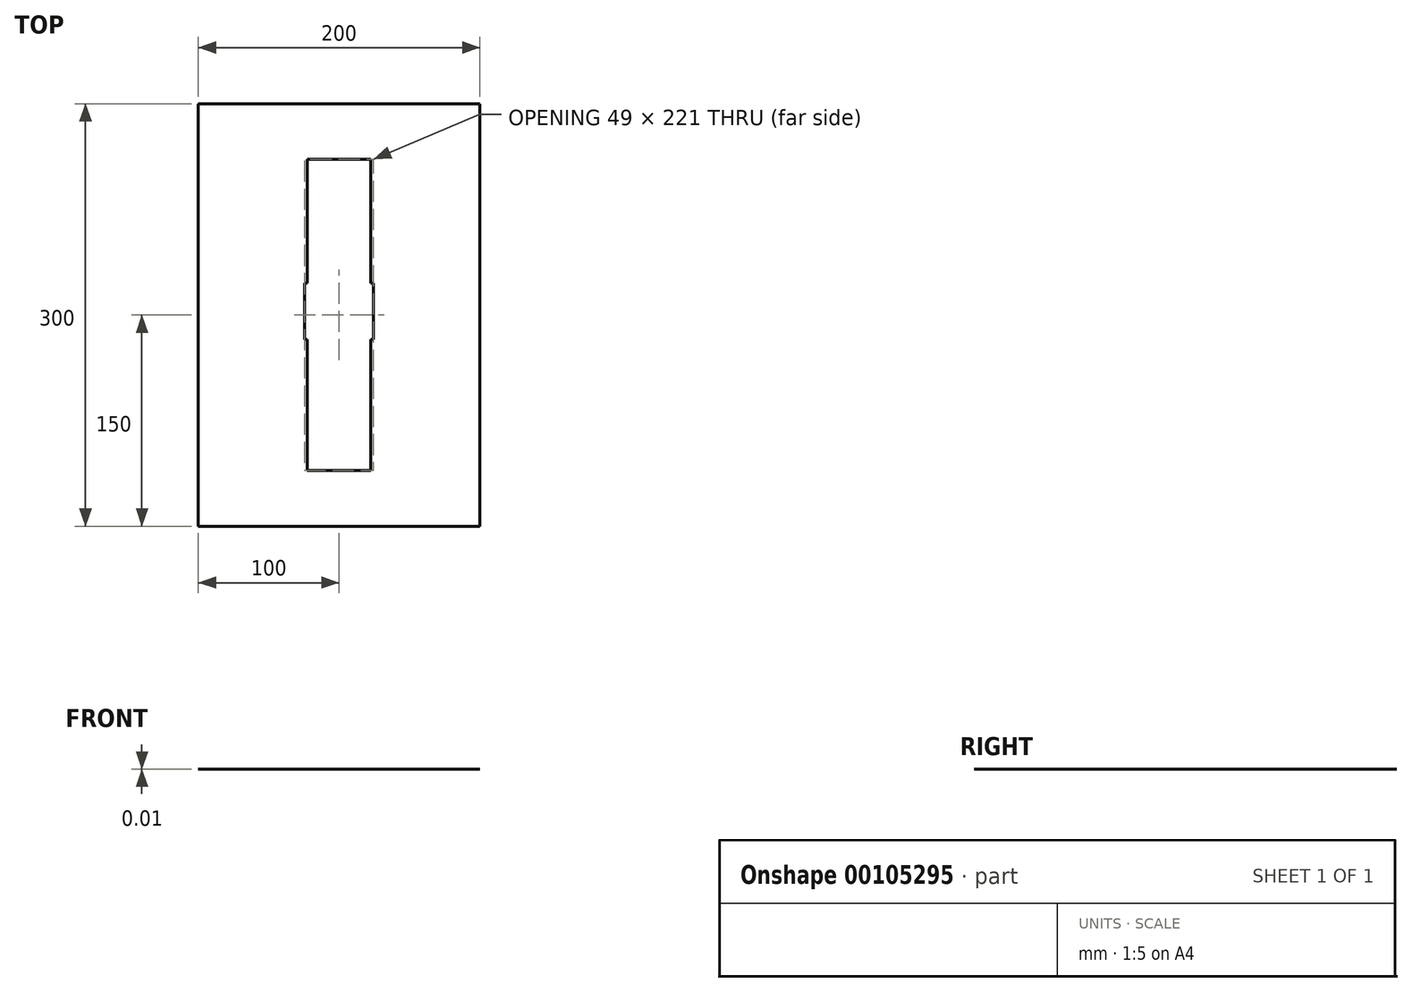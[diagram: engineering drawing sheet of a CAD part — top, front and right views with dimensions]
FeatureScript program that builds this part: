
annotation { "Feature Type Name" : "Feature", "Feature Type Description" : "" }
export const myFeature = defineFeature(function(context is Context, id is Id, definition is map)
    precondition{}
    {
        {
            var Q0;
            Q0=qCreatedBy(makeId("Top.planeOp"),FACE);
            var sketch = newSketch(context, id + "F0", { "sketchPlane" : qUnion([Q0])});
            skLineSegment(sketch, "E0.bottom", {"start": v(-100, -150) * mm, "end": v(100, -150) * mm});
            skLineSegment(sketch, "E0.top", {"start": v(-100, 150) * mm, "end": v(100, 150) * mm});
            skLineSegment(sketch, "E0.left", {"start": v(-100, -150) * mm, "end": v(-100, 150) * mm});
            skLineSegment(sketch, "E0.right", {"start": v(100, -150) * mm, "end": v(100, 150) * mm});
            skPoint(sketch, "E0.middle", {"position": v(0, 0) * mm});
            skSolve(sketch);
        }
        {
            var Q0;
            Q0 = qSketchRegion(id + "F0", true);
            extrude(context, id + "F1", {"entities" : qUnion([Q0]), "depth" : 1 / 101.6 * mm});
        }
        {
            var Q0;
            Q0=makeQuery(id+"F1.opExtrude","CAP_FACE",FACE,{"disambiguationData":[OSD([sQuery(id+"F0.wireOp",EDGE,"E0.bottom"),sQuery(id+"F0.wireOp",EDGE,"E0.top"),sQuery(id+"F0.wireOp",EDGE,"E0.left"),sQuery(id+"F0.wireOp",EDGE,"E0.right")])],"isStart":false});
            var sketch = newSketch(context, id + "F2", { "sketchPlane" : qUnion([Q0])});
            skLineSegment(sketch, "E1.bottom", {"start": v(22.5, 110.5) * mm, "end": v(-22.5, 110.5) * mm});
            skLineSegment(sketch, "E1.top", {"start": v(22.5, -110.5) * mm, "end": v(-22.5, -110.5) * mm});
            skLineSegment(sketch, "E1.left", {"start": v(22.5, 110.5) * mm, "end": v(22.5, -110.5) * mm});
            skLineSegment(sketch, "E1.right", {"start": v(-22.5, 110.5) * mm, "end": v(-22.5, -110.5) * mm});
            skPoint(sketch, "E1.middle", {"position": v(0, 0) * mm});
            skLineSegment(sketch, "E2.bottom", {"start": v(22.5, -17.52) * mm, "end": v(24.5, -17.52) * mm});
            skLineSegment(sketch, "E2.top", {"start": v(22.5, 22.48) * mm, "end": v(24.5, 22.48) * mm});
            skLineSegment(sketch, "E2.left", {"start": v(22.5, -17.52) * mm, "end": v(22.5, 22.48) * mm});
            skLineSegment(sketch, "E2.right", {"start": v(24.5, -17.52) * mm, "end": v(24.5, 22.48) * mm});
            skLineSegment(sketch, "E3.bottom", {"start": v(-22.5, 22.48) * mm, "end": v(-24.5, 22.48) * mm});
            skLineSegment(sketch, "E3.top", {"start": v(-22.5, -17.52) * mm, "end": v(-24.5, -17.52) * mm});
            skLineSegment(sketch, "E3.left", {"start": v(-22.5, 22.48) * mm, "end": v(-22.5, -17.52) * mm});
            skLineSegment(sketch, "E3.right", {"start": v(-24.5, 22.48) * mm, "end": v(-24.5, -17.52) * mm});
            skSolve(sketch);
        }
        {
            var Q0;
            Q0 = qSketchRegion(id + "F2", true);
            extrude(context, id + "F3", {"entities" : qUnion([Q0]), "operationType" : NewBodyOperationType.REMOVE, "oppositeDirection" : true, "depth" : 25.4 * mm});
        }
    });
